# Revit family: Folding-Doors_Series-9200_4-Panel_All-Weather
name_source: partatom
category: Doors
units: mm (PartAtom-declared; Revit-internal decimal feet)

## family parameters
Always vertical = Yes
Classification Number = 23.30.10.14.11
Cut with Voids When Loaded = No
Host = Wall
Room Calculation Point = No
Shared = No

## types (3) — shared parameters
ADA Compliant = Yes
Analytic Construction = <None>
Define Thermal Properties by = Schematic Type
Door Glazing = Glass - Clear
Frame Finish = Metal - Stainless Steel
Frame Thickness = 0' - 6 1/8"
Frame Width = 0' - 2 3/4"
Function = Interior
Hardware Finish = Metal - Steel
Panel Material = Metal - Stainless Steel
Rough Width = 14' - 0"
Stop Depth = 0' - 0 5/8"
Thickness = 0' - 2 5/8"
Wall Closure = By host
Width = 14' - 0"
zero-valued in all types: Expected Lifespan (Years), Maintenance Schedule (Months), R_Value, Sound Transmission Class (STC), Warranty Duration (Years)

## per-type parameters (varying)
| type | Height | Panel Height | Rough Height |
| 081316_4461-116 | 9' - 8" | 9' - 8" | 9' - 8" |
| 081316_4461-117 | 9' - 9" | 9' - 9" | 9' - 9" |
| 081316_4461-118 | 9' - 10" | 9' - 10" | 9' - 10" |

## geometry (parser evidence)
native form markers: Sweep x13
no freeform markers — native parametric forms only
